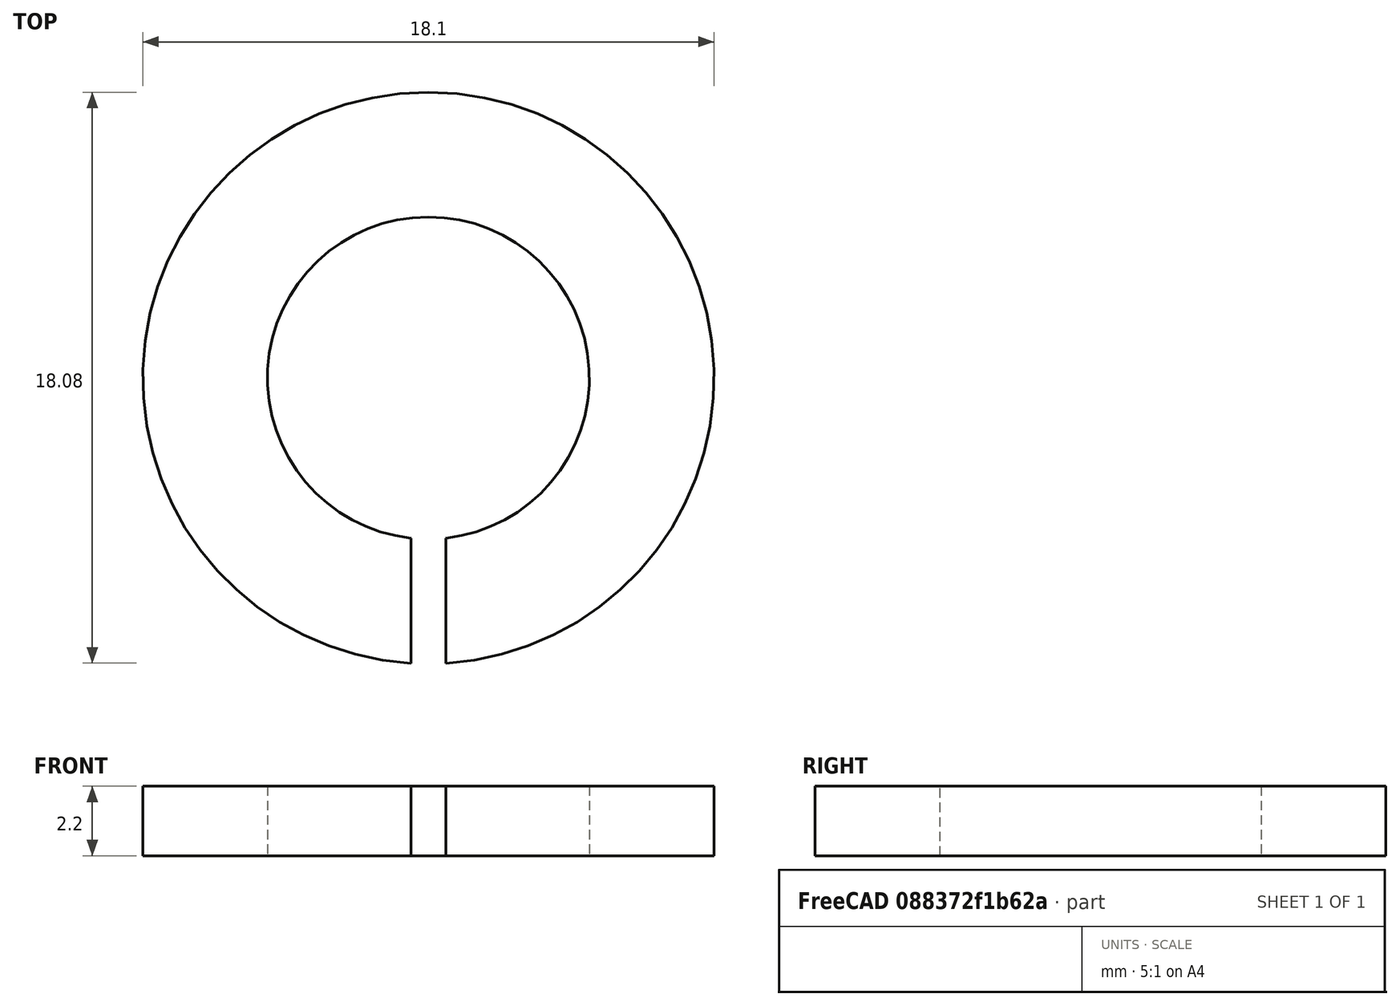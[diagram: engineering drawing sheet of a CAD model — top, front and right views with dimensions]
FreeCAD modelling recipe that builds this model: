
FCSTD DOCUMENT  (FreeCAD 0.15R4651 (Git))
Label: Federring_DIN127-A10
License: All rights reserved
LicenseURL: http://de.wikipedia.org/wiki/Alle_Rechte_vorbehalten
objects: Sketcher::SketchObject×1, PartDesign::Pad×1
note: 3 computed .brp shape members not serialized (recipe doc carries the construction recipe); baked Part::Feature solids carry a one-line shape summary decoded from their .brp

FEATURE [Sketcher::SketchObject] Sketch
  sketch-geometry (4):
    g0: ArcOfCircle CenterX=0 CenterY=0 CenterZ=0 NormalX=0 NormalY=0 NormalZ=1 Radius=5.1 StartAngle=4.82044 EndAngle=10.8875
    g1: ArcOfCircle CenterX=0 CenterY=0 CenterZ=0 NormalX=0 NormalY=0 NormalZ=1 Radius=9.05 StartAngle=4.7732 EndAngle=10.9348
    g2: LineSegment StartX=0.55 StartY=-5.07026 StartZ=0 EndX=0.55 EndY=-9.03327 EndZ=0
    g3: LineSegment StartX=-0.55 StartY=-9.03327 StartZ=0 EndX=-0.55 EndY=-5.07026 EndZ=0
  constraints (12):
    c: Coincident(g0,g-1)
    c: Coincident(g1,g-1)
    c: Vertical(g2)
    c: Vertical(g3)
    c: Coincident(g0,g2)
    c: Coincident(g0,g3)
    c: Coincident(g1,g2)
    c: Coincident(g1,g3)
    c: Symmetric(g1,g1,g-2)
    c: Radius(g0) = 5.1
    c: Radius(g1) = 9.05
    c: DistanceX(g1,g1) = -1.1
FEATURE [PartDesign::Pad] Pad  label="Federring DIN 127-A 10 #"
  Length = 2.2
  Length2 = 100
  Midplane = true
  Sketch = -> Sketch
  Type = 0
